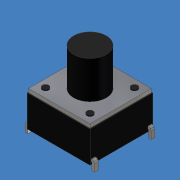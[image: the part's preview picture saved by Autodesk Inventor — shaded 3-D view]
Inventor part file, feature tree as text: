
AUTODESK INVENTOR PART (.ipt)
format: ipt  version: 2011 (Build 150239000, 239)  size: 151,040 bytes
history: native  units: mm (DEFAULTED — no unit token found)
features: sketch x6, extrude x4, mirror x2, pattern_circular x1, plane x1, sweep x1
ambient origin geometry x8: Origin, YZ Plane, XZ Plane, XY Plane, X Axis, Y Axis, Z Axis, Center Point
bodies: Solid1 (feature_tree)
feature tree (15):
  extrude  "Extrusion1"  Depth=3.175mm TaperAngle=0.0deg
  extrude  "Extrusion2"  Depth=4.1656mm TaperAngle=0.0deg
  extrude  "Extrusion3"  Depth=0.508mm TaperAngle=0.0deg
  pattern_circular  "Circular Pattern1"  Count=4 Angle=360.0deg
  extrude  "Extrusion4"  Depth=0.381mm
  sketch  "Sketch5"  dims[d15=0.254mm d16=0.127mm]
  plane  "Work Plane1"
  sweep  "Sweep1"
  mirror  "Mirror1"
  mirror  "Mirror2"
  sketch  "Sketch1"  dims[d0=6.35mm d1=3.175mm d2=0.0mm]
  sketch  "Sketch2"  dims[d3=3.302mm d4=4.1656mm d5=0.0mm]
  sketch  "Sketch3"  dims[d6=0.635mm d7=0.508mm d8=0.0mm d9=40.0mm d11=360.0deg]
  sketch  "Sketch4"  dims[d12=0.381mm d13=0.0mm d14=0.381mm]
  sketch  "Sketch6"  dims[d17=0.254mm d18=90.0deg d19=0.508mm d20=1.016mm d21=0.254mm d22=0.0mm]
